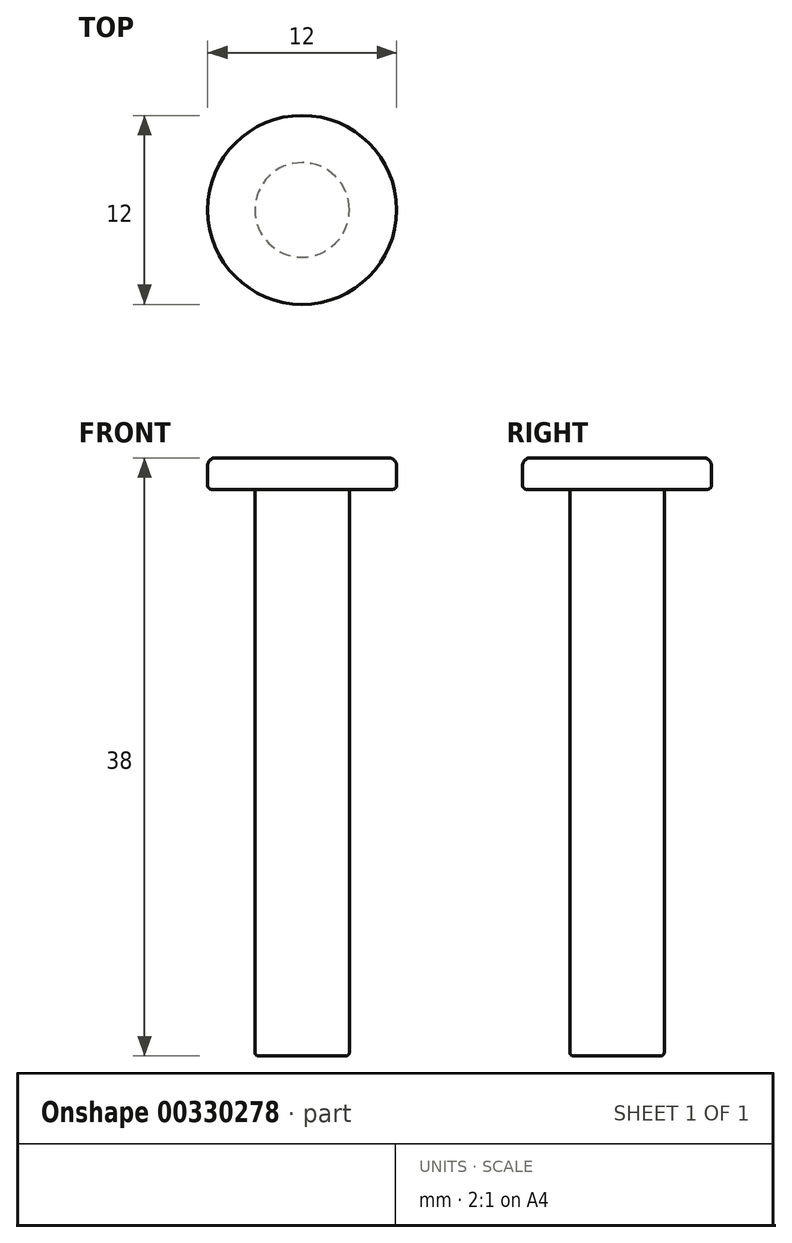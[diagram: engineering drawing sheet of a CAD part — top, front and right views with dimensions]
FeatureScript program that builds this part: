
annotation { "Feature Type Name" : "Feature", "Feature Type Description" : "" }
export const myFeature = defineFeature(function(context is Context, id is Id, definition is map)
    precondition{}
    {
        {
            var Q0;
            Q0=qCreatedBy(makeId("Top.planeOp"),FACE);
            var sketch = newSketch(context, id + "F0", { "sketchPlane" : qUnion([Q0])});
            skCircle(sketch, "E0", {"center": v(0, 0) * mm, "radius": 3 * mm});
            skSolve(sketch);
        }
        {
            var Q0;
            Q0 = qSketchRegion(id + "F0", true);
            extrude(context, id + "F1", {"entities" : qUnion([Q0]), "depth" : 36 * mm});
        }
        {
            var Q0;
            Q0=makeQuery(id+"F1.opExtrude","CAP_FACE",FACE,{"disambiguationData":[OSD([sQuery(id+"F0.wireOp",EDGE,"E0")])],"isStart":false});
            var sketch = newSketch(context, id + "F2", { "sketchPlane" : qUnion([Q0])});
            skCircle(sketch, "E1", {"center": v(0, 0) * mm, "radius": 6 * mm});
            skSolve(sketch);
        }
        {
            var Q0;
            Q0 = qSketchRegion(id + "F2", true);
            extrude(context, id + "F3", {"entities" : qUnion([Q0]), "operationType" : NewBodyOperationType.ADD, "depth" : 2 * mm});
        }
        {
            var Q0;
            Q0=makeQuery(id+"F3.opExtrude","CAP_EDGE",EDGE,{"disambiguationData":[OSD([sQuery(id+"F2.wireOp",EDGE,"E1")])],"isStart":false});
            fillet(context, id + "F4", {"entities" : qUnion([Q0]), "radius" : 0.5 * mm, "tangentPropagation" : true, "allowEdgeOverflow" : false});
        }
        {
            var Q0;
            Q0=makeQuery(id+"F3.opExtrude","CAP_EDGE",EDGE,{"disambiguationData":[OSD([sQuery(id+"F2.wireOp",EDGE,"E1")])],"isStart":true});
            var Q1;
            Q1=makeQuery(id+"F1.opExtrude","CAP_EDGE",EDGE,{"disambiguationData":[OSD([sQuery(id+"F0.wireOp",EDGE,"E0")])],"isStart":true});
            fillet(context, id + "F5", {"entities" : qUnion([Q0, Q1]), "radius" : 0.25 * mm, "tangentPropagation" : true, "allowEdgeOverflow" : false});
        }
    });
